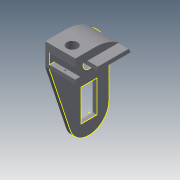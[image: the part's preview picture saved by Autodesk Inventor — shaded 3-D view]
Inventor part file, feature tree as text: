
AUTODESK INVENTOR PART (.ipt)
format: ipt  version: 2013 (Build 170138000, 138)  size: 280,576 bytes
history: native  units: mm
features: sketch x21, extrude x17
ambient origin geometry x8: Origin, YZ Plane, XZ Plane, XY Plane, X Axis, Y Axis, Z Axis, Center Point
bodies: Solid1 (feature_tree)
feature tree (38):
  extrude  "Extrusion1"  Depth=66.3mm
  extrude  "Extrusion2"  Depth=55.0mm
  extrude  "Extrusion3"  Depth=55.0mm
  extrude  "Extrusion4"  Depth=9.9mm
  extrude  "Extrusion5"  Depth=9.9mm
  extrude  "Extrusion6"  Depth=3.0mm
  extrude  "Extrusion7"  Depth=3.0mm
  extrude  "Extrusion8"  Depth=13.6mm
  extrude  "Extrusion9"  Depth=45.0mm
  sketch  "Sketch10"  dims[d22=15.0mm d23=5.0mm d24=0.0mm]
  extrude  "Extrusion10"  Depth=5.0mm TaperAngle=0.0deg
  extrude  "Extrusion11"  Depth=55.0mm
  extrude  "Extrusion12"  Depth=20.0mm
  sketch  "Sketch14"  dims[d33=10.0mm d34=32.9mm d35=0.0mm]
  extrude  "Extrusion13"  Depth=5.0mm TaperAngle=0.0deg
  extrude  "Extrusion14"  Depth=32.9mm TaperAngle=0.0deg
  extrude  "Extrusion15"  Depth=25.0mm
  extrude  "Extrusion16"  Depth=5.0mm TaperAngle=0.0deg
  extrude  "Extrusion17"  Depth=15.0mm
  sketch  "Sketch20"  dims[d47=5.0mm]
  sketch  "Sketch21"  dims[d48=32.9mm d49=0.0mm d50=28.0mm d51=5.0mm d52=0.0mm d53=10.0mm d54=0.0mm d55=5.0mm d56=12.5mm d57=13.6mm d58=10.0mm d59=0.0mm d60=12.5mm d61=12.4mm d62=12.2mm d63=6.2mm d64=5.0mm d65=0.0mm d66=10.6mm d67=2.0mm d68=21.4mm d69=2.0mm d70=5.0mm d71=0.0mm d72=2.05mm d73=2.05mm d74=5.0mm d75=0.0mm d76=21.4mm d77=2.05mm d78=2.0mm d79=10.6mm d80=2.05mm d81=2.0mm d82=5.0mm d83=0.0mm d84=45.0mm d86=5.0mm d87=5.0mm d88=39.0mm d89=0.0mm d90=22.0mm d91=5.0mm d92=0.0mm]
  sketch  "Sketch1"  dims[d0=33.15mm d2=66.3mm]
  sketch  "Sketch2"  dims[d4=18.1mm d5=55.0mm]
  sketch  "Sketch3"  dims[d6=20.0mm d7=55.0mm]
  sketch  "Sketch4"  dims[d8=40.2mm d9=9.9mm]
  sketch  "Sketch5"  dims[d10=9.5mm d11=9.9mm]
  sketch  "Sketch6"  dims[d12=9.5mm d13=3.0mm]
  sketch  "Sketch7"  dims[d14=3.0mm d15=3.0mm]
  sketch  "Sketch8"  dims[d16=3.0mm d17=13.6mm]
  sketch  "Sketch9"  dims[d20=25.0mm d21=45.0mm]
  sketch  "Sketch11"  dims[d25=18.1mm d26=55.0mm]
  sketch  "Sketch12"  dims[d27=40.2mm d28=20.0mm]
  sketch  "Sketch13"  dims[d29=5.0mm d30=0.0mm d31=5.0mm d32=0.0mm]
  sketch  "Sketch15"  dims[d36=25.0mm d37=0.0mm d38=25.0mm]
  sketch  "Sketch16"  dims[d39=10.0mm d40=5.0mm d41=0.0mm]
  sketch  "Sketch17"  dims[d42=12.5mm d43=15.0mm]
  sketch  "Sketch18"  dims[d44=10.0mm d45=0.0mm]
  sketch  "Sketch19"  dims[d46=18.0mm]
